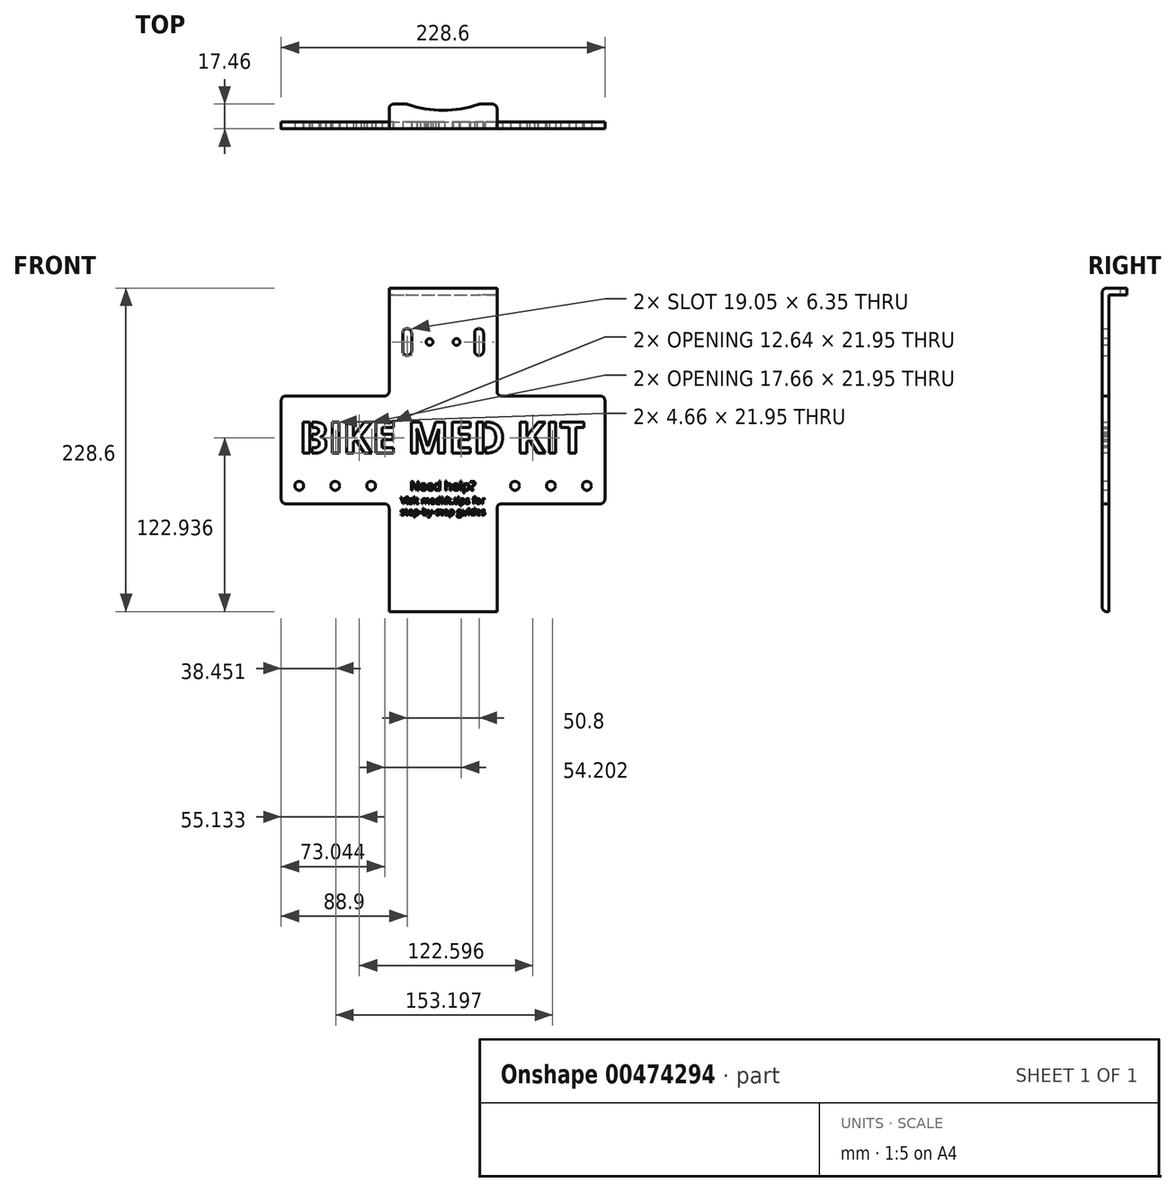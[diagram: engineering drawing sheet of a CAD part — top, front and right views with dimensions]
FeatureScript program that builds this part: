
annotation { "Feature Type Name" : "Feature", "Feature Type Description" : "" }
export const myFeature = defineFeature(function(context is Context, id is Id, definition is map)
    precondition{}
    {
        {
            var Q0;
            Q0=qCreatedBy(makeId("Front.planeOp"),FACE);
            var sketch = newSketch(context, id + "F0", { "sketchPlane" : qUnion([Q0])});
            skLineSegment(sketch, "E0.bottom", {"start": v(-38.1, 114.3) * mm, "end": v(38.1, 114.3) * mm});
            skLineSegment(sketch, "E0.top", {"start": v(-38.1, -114.3) * mm, "end": v(38.1, -114.3) * mm});
            skLineSegment(sketch, "E0.left", {"start": v(-38.1, 114.3) * mm, "end": v(-38.1, 38.1) * mm});
            skLineSegment(sketch, "E0.right", {"start": v(38.1, 114.3) * mm, "end": v(38.1, 38.1) * mm});
            skPoint(sketch, "E0.middle", {"position": v(0, 0) * mm});
            skLineSegment(sketch, "E1.bottom", {"start": v(114.3, 38.1) * mm, "end": v(38.1, 38.1) * mm});
            skLineSegment(sketch, "E1.top", {"start": v(114.3, -38.1) * mm, "end": v(38.1, -38.1) * mm});
            skLineSegment(sketch, "E1.left", {"start": v(114.3, 38.1) * mm, "end": v(114.3, -38.1) * mm});
            skLineSegment(sketch, "E1.right", {"start": v(-114.3, 38.1) * mm, "end": v(-114.3, -38.1) * mm});
            skLineSegment(sketch, "E2.trimOffspring", {"start": v(-38.1, 38.1) * mm, "end": v(-114.3, 38.1) * mm});
            skLineSegment(sketch, "E3.trimOffspring", {"start": v(-38.1, -38.1) * mm, "end": v(-38.1, -114.3) * mm});
            skLineSegment(sketch, "E4.trimOffspring", {"start": v(-38.1, -38.1) * mm, "end": v(-114.3, -38.1) * mm});
            skLineSegment(sketch, "E5.trimOffspring", {"start": v(38.1, -38.1) * mm, "end": v(38.1, -114.3) * mm});
            skSolve(sketch);
        }
        {
            var Q0;
            Q0=qSketchRegion(id+"F0",true);
            extrude(context, id + "F1", {"entities" : qUnion([Q0]), "oppositeDirection" : true, "depth" : 4.76 * mm});
        }
        {
            var Q0;
            Q0=makeQuery(id+"F1.opExtrude","CAP_FACE",FACE,{"disambiguationData":[OSD([sQuery(id+"F0.wireOp",EDGE,"E0.bottom"),sQuery(id+"F0.wireOp",EDGE,"E0.top"),sQuery(id+"F0.wireOp",EDGE,"E0.left"),sQuery(id+"F0.wireOp",EDGE,"E0.right"),sQuery(id+"F0.wireOp",EDGE,"E1.bottom"),sQuery(id+"F0.wireOp",EDGE,"E1.top"),sQuery(id+"F0.wireOp",EDGE,"E1.left"),sQuery(id+"F0.wireOp",EDGE,"E1.right"),sQuery(id+"F0.wireOp",EDGE,"E2.trimOffspring"),sQuery(id+"F0.wireOp",EDGE,"E3.trimOffspring"),sQuery(id+"F0.wireOp",EDGE,"E4.trimOffspring"),sQuery(id+"F0.wireOp",EDGE,"E5.trimOffspring")])],"isStart":true});
            var sketch = newSketch(context, id + "F2", { "sketchPlane" : qUnion([Q0])});
            skCircle(sketch, "E6", {"center": v(-101.6, -25.4) * mm, "radius": 3.18 * mm});
            skCircle(sketch, "E7.1.0.0", {"center": v(-76.2, -25.4) * mm, "radius": 3.18 * mm});
            skLineSegment(sketch, "E7.direction1", {"start": v(-101.6, -25.4) * mm, "end": v(-76.2, -25.4) * mm, "construction": true});
            skCircle(sketch, "E8", {"center": v(101.6, -25.4) * mm, "radius": 3.18 * mm});
            skCircle(sketch, "E9.1.0.0", {"center": v(76.2, -25.4) * mm, "radius": 3.18 * mm});
            skLineSegment(sketch, "E9.direction1", {"start": v(101.6, -25.4) * mm, "end": v(76.2, -25.4) * mm, "construction": true});
            skCircle(sketch, "E10.0.2.0", {"center": v(-50.8, -25.4) * mm, "radius": 3.18 * mm});
            skCircle(sketch, "E11.0.2.0", {"center": v(50.8, -25.4) * mm, "radius": 3.18 * mm});
            skSolve(sketch);
        }
        {
            var Q0;
            Q0=qSketchRegion(id+"F2",true);
            extrude(context, id + "F3", {"entities" : qUnion([Q0]), "operationType" : NewBodyOperationType.REMOVE, "endBound" : BoundingType.THROUGH_ALL, "oppositeDirection" : true, "depth" : 25.4 * mm});
        }
        {
            var Q0;
            Q0=makeQuery(id+"F1.opExtrude","CAP_FACE",FACE,{"disambiguationData":[OSD([sQuery(id+"F0.wireOp",EDGE,"E0.bottom"),sQuery(id+"F0.wireOp",EDGE,"E0.top"),sQuery(id+"F0.wireOp",EDGE,"E0.left"),sQuery(id+"F0.wireOp",EDGE,"E0.right"),sQuery(id+"F0.wireOp",EDGE,"E1.bottom"),sQuery(id+"F0.wireOp",EDGE,"E1.top"),sQuery(id+"F0.wireOp",EDGE,"E1.left"),sQuery(id+"F0.wireOp",EDGE,"E1.right"),sQuery(id+"F0.wireOp",EDGE,"E2.trimOffspring"),sQuery(id+"F0.wireOp",EDGE,"E3.trimOffspring"),sQuery(id+"F0.wireOp",EDGE,"E4.trimOffspring"),sQuery(id+"F0.wireOp",EDGE,"E5.trimOffspring")])],"isStart":true});
            var sketch = newSketch(context, id + "F4", { "sketchPlane" : qUnion([Q0])});
            skText(sketch, "E12", { "text": "BIKE MED KIT", "fontName": "OpenSans-Bold.ttf"});
            skLineSegment(sketch, "E13", {"start": v(-101.6, -22.23) * mm, "end": v(-76.2, -22.23) * mm, "construction": true});
            skLineSegment(sketch, "E14", {"start": v(-101.6, 7.94) * mm, "end": v(101.6, 7.94) * mm, "construction": true});
            const initialGuessF4  = {"E12": [-0.1016, -0.00234, 1, 0, 0.02214]};
            skSetInitialGuess(sketch, initialGuessF4);
            skSolve(sketch);
        }
        {
            var Q0;
            Q0=qSketchRegion(id+"F4",true);
            extrude(context, id + "F5", {"entities" : qUnion([Q0]), "operationType" : NewBodyOperationType.REMOVE, "endBound" : BoundingType.THROUGH_ALL, "oppositeDirection" : true, "depth" : 25.4 * mm});
        }
        {
            var Q0;
            {var subQ0=sQuery(id+"F0.wireOp",EDGE,"E2.trimOffspring");var subQ1=sQuery(id+"F0.wireOp",EDGE,"E1.right");var subQ2=sQuery(id+"F0.wireOp",EDGE,"E5.trimOffspring");var subQ3=sQuery(id+"F0.wireOp",EDGE,"E1.top");var subQ4=sQuery(id+"F0.wireOp",EDGE,"E1.left");var subQ5=sQuery(id+"F0.wireOp",EDGE,"E0.left");var subQ6=sQuery(id+"F0.wireOp",EDGE,"E1.bottom");var subQ7=sQuery(id+"F0.wireOp",EDGE,"E4.trimOffspring");var subQ8=sQuery(id+"F0.wireOp",EDGE,"E0.top");var subQ9=sQuery(id+"F0.wireOp",EDGE,"E0.right");var subQ10=sQuery(id+"F0.wireOp",EDGE,"E0.bottom");var subQ11=sQuery(id+"F0.wireOp",EDGE,"E3.trimOffspring");Q0=makeQuery(id+"F5.boolean.opBoolean","SPLIT",FACE,{"disambiguationData":[TD([makeQuery(id+"F1.opExtrude","SWEPT_FACE",FACE,{"disambiguationData":[OSD([subQ10])]})])],"derivedFrom":makeQuery(id+"F1.opExtrude","CAP_FACE",FACE,{"disambiguationData":[OSD([subQ10,subQ8,subQ5,subQ9,subQ6,subQ3,subQ4,subQ1,subQ0,subQ11,subQ7,subQ2])],"isStart":true})});}
            var sketch = newSketch(context, id + "F6", { "sketchPlane" : qUnion([Q0])});
            skLineSegment(sketch, "E15.bottom", {"start": v(-94.18, 23) * mm, "end": v(-92.6, 23) * mm});
            skLineSegment(sketch, "E15.top", {"start": v(-94.18, -7.38) * mm, "end": v(-92.6, -7.38) * mm});
            skLineSegment(sketch, "E15.left", {"start": v(-94.18, 23) * mm, "end": v(-94.18, -7.38) * mm});
            skLineSegment(sketch, "E15.right", {"start": v(-92.6, 23) * mm, "end": v(-92.6, -7.38) * mm});
            skLineSegment(sketch, "E16.bottom", {"start": v(28.49, 25.23) * mm, "end": v(30.07, 25.23) * mm});
            skLineSegment(sketch, "E16.top", {"start": v(28.49, -11.56) * mm, "end": v(30.07, -11.56) * mm});
            skLineSegment(sketch, "E16.left", {"start": v(28.49, 25.23) * mm, "end": v(28.49, -11.56) * mm});
            skLineSegment(sketch, "E16.right", {"start": v(30.07, 25.23) * mm, "end": v(30.07, -11.56) * mm});
            skSolve(sketch);
        }
        {
            var Q0;
            Q0=qSketchRegion(id+"F6",true);
            var Q1;
            {var subQ0=sQuery(id+"F0.wireOp",EDGE,"E2.trimOffspring");var subQ1=sQuery(id+"F0.wireOp",EDGE,"E1.right");var subQ2=sQuery(id+"F0.wireOp",EDGE,"E5.trimOffspring");var subQ3=sQuery(id+"F0.wireOp",EDGE,"E1.top");var subQ4=sQuery(id+"F0.wireOp",EDGE,"E1.left");var subQ5=sQuery(id+"F0.wireOp",EDGE,"E0.left");var subQ6=sQuery(id+"F0.wireOp",EDGE,"E1.bottom");var subQ7=sQuery(id+"F0.wireOp",EDGE,"E4.trimOffspring");var subQ8=sQuery(id+"F0.wireOp",EDGE,"E0.top");var subQ9=sQuery(id+"F0.wireOp",EDGE,"E0.right");var subQ10=sQuery(id+"F0.wireOp",EDGE,"E0.bottom");var subQ11=sQuery(id+"F0.wireOp",EDGE,"E3.trimOffspring");Q1=makeQuery(id+"F5.boolean.opBoolean","SPLIT",FACE,{"disambiguationData":[TD([makeQuery(id+"F1.opExtrude","SWEPT_FACE",FACE,{"disambiguationData":[OSD([subQ10])]})])],"derivedFrom":makeQuery(id+"F1.opExtrude","CAP_FACE",FACE,{"disambiguationData":[OSD([subQ10,subQ8,subQ5,subQ9,subQ6,subQ3,subQ4,subQ1,subQ0,subQ11,subQ7,subQ2])],"isStart":false})});}
            extrude(context, id + "F7", {"entities" : qUnion([Q0]), "operationType" : NewBodyOperationType.ADD, "endBound" : BoundingType.UP_TO_SURFACE, "oppositeDirection" : true, "endBoundEntityFace" : qUnion([Q1]), "depth" : 25.4 * mm});
        }
        {
            var Q0;
            {var subQ0=sQuery(id+"F0.wireOp",EDGE,"E5.trimOffspring");var subQ1=sQuery(id+"F0.wireOp",EDGE,"E4.trimOffspring");var subQ2=sQuery(id+"F0.wireOp",EDGE,"E3.trimOffspring");var subQ3=sQuery(id+"F0.wireOp",EDGE,"E2.trimOffspring");var subQ4=sQuery(id+"F0.wireOp",EDGE,"E1.right");var subQ5=sQuery(id+"F0.wireOp",EDGE,"E1.left");var subQ6=sQuery(id+"F0.wireOp",EDGE,"E1.top");var subQ7=sQuery(id+"F0.wireOp",EDGE,"E1.bottom");var subQ8=sQuery(id+"F0.wireOp",EDGE,"E0.right");var subQ9=sQuery(id+"F0.wireOp",EDGE,"E0.left");var subQ10=sQuery(id+"F0.wireOp",EDGE,"E0.top");var subQ11=sQuery(id+"F0.wireOp",EDGE,"E0.bottom");var subQ12=makeQuery(id+"F1.opExtrude","CAP_FACE",FACE,{"disambiguationData":[OSD([subQ11,subQ10,subQ9,subQ8,subQ7,subQ6,subQ5,subQ4,subQ3,subQ2,subQ1,subQ0])],"isStart":true});Q0=makeQuery(id+"F7.boolean.opBoolean","MERGE",FACE,{"derivedFrom":[makeQuery(id+"F5.boolean.opBoolean","SPLIT",FACE,{"disambiguationData":[TD([makeQuery(id+"F1.opExtrude","SWEPT_FACE",FACE,{"disambiguationData":[OSD([subQ11])]})])],"derivedFrom":subQ12}),makeQuery(id+"F5.boolean.opBoolean","SPLIT",FACE,{"disambiguationData":[TD([makeQuery(id+"F5.opExtrude","SWEPT_FACE",FACE,{"disambiguationData":[OSD([sQuery(id+"F4.wireOp",EDGE,"E12.sketch_text.stroke-12")])]})])],"derivedFrom":subQ12}),makeQuery(id+"F5.boolean.opBoolean","SPLIT",FACE,{"disambiguationData":[TD([makeQuery(id+"F5.opExtrude","SWEPT_FACE",FACE,{"disambiguationData":[OSD([sQuery(id+"F4.wireOp",EDGE,"E12.sketch_text.stroke-19")])]})])],"derivedFrom":subQ12}),makeQuery(id+"F5.boolean.opBoolean","SPLIT",FACE,{"disambiguationData":[TD([makeQuery(id+"F5.opExtrude","SWEPT_FACE",FACE,{"disambiguationData":[OSD([sQuery(id+"F4.wireOp",EDGE,"E12.sketch_text.stroke-92")])]})])],"derivedFrom":subQ12}),makeQuery(id+"F7.opExtrude","CAP_FACE",FACE,{"disambiguationData":[OSD([sQuery(id+"F6.wireOp",EDGE,"E15.bottom"),sQuery(id+"F6.wireOp",EDGE,"E15.top"),sQuery(id+"F6.wireOp",EDGE,"E15.left"),sQuery(id+"F6.wireOp",EDGE,"E15.right")])],"isStart":true}),makeQuery(id+"F7.opExtrude","CAP_FACE",FACE,{"disambiguationData":[OSD([sQuery(id+"F6.wireOp",EDGE,"E16.bottom"),sQuery(id+"F6.wireOp",EDGE,"E16.top"),sQuery(id+"F6.wireOp",EDGE,"E16.left"),sQuery(id+"F6.wireOp",EDGE,"E16.right")])],"isStart":true})]});}
            var sketch = newSketch(context, id + "F8", { "sketchPlane" : qUnion([Q0])});
            skLineSegment(sketch, "E17.bottom", {"start": v(-28.57, 85.73) * mm, "end": v(-22.22, 85.73) * mm});
            skLineSegment(sketch, "E17.top", {"start": v(-28.57, 66.68) * mm, "end": v(-22.22, 66.68) * mm});
            skLineSegment(sketch, "E17.left", {"start": v(-28.57, 85.73) * mm, "end": v(-28.57, 66.68) * mm});
            skLineSegment(sketch, "E17.right", {"start": v(-22.22, 85.73) * mm, "end": v(-22.22, 66.68) * mm});
            skLineSegment(sketch, "E18.MirrorCS", {"start": v(22.22, 85.73) * mm, "end": v(22.22, 66.68) * mm});
            skLineSegment(sketch, "E19.MirrorCS", {"start": v(28.57, 66.67) * mm, "end": v(22.22, 66.67) * mm});
            skLineSegment(sketch, "E20.MirrorCS", {"start": v(28.57, 85.73) * mm, "end": v(28.57, 66.67) * mm});
            skLineSegment(sketch, "E21.MirrorCS", {"start": v(28.57, 85.73) * mm, "end": v(22.22, 85.73) * mm});
            skLineSegment(sketch, "E22", {"start": v(-28.57, 76.2) * mm, "end": v(-22.22, 76.2) * mm, "construction": true});
            skLineSegment(sketch, "E23", {"start": v(-25.4, 85.73) * mm, "end": v(-25.4, 66.68) * mm, "construction": true});
            skSolve(sketch);
        }
        {
            var Q0;
            Q0=qSketchRegion(id+"F8",true);
            extrude(context, id + "F9", {"entities" : qUnion([Q0]), "operationType" : NewBodyOperationType.REMOVE, "endBound" : BoundingType.THROUGH_ALL, "oppositeDirection" : true, "depth" : 25.4 * mm});
        }
        {
            var Q0;
            Q0=makeQuery(id+"F9.boolean.opBoolean","COPY",EDGE,{"derivedFrom":makeQuery(id+"F9.opExtrude","SWEPT_EDGE",EDGE,{"disambiguationData":[OSD([sQuery(id+"F8.wireOp",EDGE,"E17.top"),sQuery(id+"F8.wireOp",EDGE,"E17.left")])]})});
            var Q1;
            Q1=makeQuery(id+"F9.boolean.opBoolean","COPY",EDGE,{"derivedFrom":makeQuery(id+"F9.opExtrude","SWEPT_EDGE",EDGE,{"disambiguationData":[OSD([sQuery(id+"F8.wireOp",EDGE,"E17.top"),sQuery(id+"F8.wireOp",EDGE,"E17.right")])]})});
            var Q2;
            Q2=makeQuery(id+"F9.boolean.opBoolean","COPY",EDGE,{"derivedFrom":makeQuery(id+"F9.opExtrude","SWEPT_EDGE",EDGE,{"disambiguationData":[OSD([sQuery(id+"F8.wireOp",EDGE,"E19.MirrorCS"),sQuery(id+"F8.wireOp",EDGE,"E20.MirrorCS")])]})});
            var Q3;
            Q3=makeQuery(id+"F9.boolean.opBoolean","COPY",EDGE,{"derivedFrom":makeQuery(id+"F9.opExtrude","SWEPT_EDGE",EDGE,{"disambiguationData":[OSD([sQuery(id+"F8.wireOp",EDGE,"E18.MirrorCS"),sQuery(id+"F8.wireOp",EDGE,"E19.MirrorCS")])]})});
            var Q4;
            Q4=makeQuery(id+"F9.boolean.opBoolean","COPY",EDGE,{"derivedFrom":makeQuery(id+"F9.opExtrude","SWEPT_EDGE",EDGE,{"disambiguationData":[OSD([sQuery(id+"F8.wireOp",EDGE,"E18.MirrorCS"),sQuery(id+"F8.wireOp",EDGE,"E21.MirrorCS")])]})});
            var Q5;
            Q5=makeQuery(id+"F9.boolean.opBoolean","COPY",EDGE,{"derivedFrom":makeQuery(id+"F9.opExtrude","SWEPT_EDGE",EDGE,{"disambiguationData":[OSD([sQuery(id+"F8.wireOp",EDGE,"E17.bottom"),sQuery(id+"F8.wireOp",EDGE,"E17.left")])]})});
            var Q6;
            Q6=makeQuery(id+"F9.boolean.opBoolean","COPY",EDGE,{"derivedFrom":makeQuery(id+"F9.opExtrude","SWEPT_EDGE",EDGE,{"disambiguationData":[OSD([sQuery(id+"F8.wireOp",EDGE,"E17.bottom"),sQuery(id+"F8.wireOp",EDGE,"E17.right")])]})});
            var Q7;
            Q7=makeQuery(id+"F9.boolean.opBoolean","COPY",EDGE,{"derivedFrom":makeQuery(id+"F9.opExtrude","SWEPT_EDGE",EDGE,{"disambiguationData":[OSD([sQuery(id+"F8.wireOp",EDGE,"E20.MirrorCS"),sQuery(id+"F8.wireOp",EDGE,"E21.MirrorCS")])]})});
            fillet(context, id + "F10", {"entities" : qUnion([Q0, Q1, Q2, Q3, Q4, Q5, Q6, Q7]), "radius" : 3.17 * mm, "tangentPropagation" : true, "allowEdgeOverflow" : false});
        }
        {
            var Q0;
            {var subQ0=sQuery(id+"F0.wireOp",EDGE,"E5.trimOffspring");var subQ1=sQuery(id+"F0.wireOp",EDGE,"E4.trimOffspring");var subQ2=sQuery(id+"F0.wireOp",EDGE,"E3.trimOffspring");var subQ3=sQuery(id+"F0.wireOp",EDGE,"E2.trimOffspring");var subQ4=sQuery(id+"F0.wireOp",EDGE,"E1.right");var subQ5=sQuery(id+"F0.wireOp",EDGE,"E1.left");var subQ6=sQuery(id+"F0.wireOp",EDGE,"E1.top");var subQ7=sQuery(id+"F0.wireOp",EDGE,"E1.bottom");var subQ8=sQuery(id+"F0.wireOp",EDGE,"E0.right");var subQ9=sQuery(id+"F0.wireOp",EDGE,"E0.left");var subQ10=sQuery(id+"F0.wireOp",EDGE,"E0.top");var subQ11=sQuery(id+"F0.wireOp",EDGE,"E0.bottom");var subQ12=makeQuery(id+"F1.opExtrude","CAP_FACE",FACE,{"disambiguationData":[OSD([subQ11,subQ10,subQ9,subQ8,subQ7,subQ6,subQ5,subQ4,subQ3,subQ2,subQ1,subQ0])],"isStart":true});Q0=makeQuery(id+"F7.boolean.opBoolean","MERGE",FACE,{"derivedFrom":[makeQuery(id+"F5.boolean.opBoolean","SPLIT",FACE,{"disambiguationData":[TD([makeQuery(id+"F1.opExtrude","SWEPT_FACE",FACE,{"disambiguationData":[OSD([subQ11])]})])],"derivedFrom":subQ12}),makeQuery(id+"F5.boolean.opBoolean","SPLIT",FACE,{"disambiguationData":[TD([makeQuery(id+"F5.opExtrude","SWEPT_FACE",FACE,{"disambiguationData":[OSD([sQuery(id+"F4.wireOp",EDGE,"E12.sketch_text.stroke-12")])]})])],"derivedFrom":subQ12}),makeQuery(id+"F5.boolean.opBoolean","SPLIT",FACE,{"disambiguationData":[TD([makeQuery(id+"F5.opExtrude","SWEPT_FACE",FACE,{"disambiguationData":[OSD([sQuery(id+"F4.wireOp",EDGE,"E12.sketch_text.stroke-19")])]})])],"derivedFrom":subQ12}),makeQuery(id+"F5.boolean.opBoolean","SPLIT",FACE,{"disambiguationData":[TD([makeQuery(id+"F5.opExtrude","SWEPT_FACE",FACE,{"disambiguationData":[OSD([sQuery(id+"F4.wireOp",EDGE,"E12.sketch_text.stroke-92")])]})])],"derivedFrom":subQ12}),makeQuery(id+"F7.opExtrude","CAP_FACE",FACE,{"disambiguationData":[OSD([sQuery(id+"F6.wireOp",EDGE,"E15.bottom"),sQuery(id+"F6.wireOp",EDGE,"E15.top"),sQuery(id+"F6.wireOp",EDGE,"E15.left"),sQuery(id+"F6.wireOp",EDGE,"E15.right")])],"isStart":true}),makeQuery(id+"F7.opExtrude","CAP_FACE",FACE,{"disambiguationData":[OSD([sQuery(id+"F6.wireOp",EDGE,"E16.bottom"),sQuery(id+"F6.wireOp",EDGE,"E16.top"),sQuery(id+"F6.wireOp",EDGE,"E16.left"),sQuery(id+"F6.wireOp",EDGE,"E16.right")])],"isStart":true})]});}
            var sketch = newSketch(context, id + "F11", { "sketchPlane" : qUnion([Q0])});
            skCircle(sketch, "E24", {"center": v(-9.53, 76.2) * mm, "radius": 2.38 * mm});
            skCircle(sketch, "E25", {"center": v(9.53, 76.2) * mm, "radius": 2.38 * mm});
            skLineSegment(sketch, "E26", {"start": v(-22.22, 76.2) * mm, "end": v(22.22, 76.2) * mm, "construction": true});
            skSolve(sketch);
        }
        {
            var Q0;
            Q0=qSketchRegion(id+"F11",true);
            extrude(context, id + "F12", {"entities" : qUnion([Q0]), "operationType" : NewBodyOperationType.REMOVE, "endBound" : BoundingType.THROUGH_ALL, "oppositeDirection" : true, "depth" : 25.4 * mm});
        }
        {
            var Q0;
            {var subQ0=sQuery(id+"F0.wireOp",EDGE,"E5.trimOffspring");var subQ1=sQuery(id+"F0.wireOp",EDGE,"E4.trimOffspring");var subQ2=sQuery(id+"F0.wireOp",EDGE,"E3.trimOffspring");var subQ3=sQuery(id+"F0.wireOp",EDGE,"E2.trimOffspring");var subQ4=sQuery(id+"F0.wireOp",EDGE,"E1.right");var subQ5=sQuery(id+"F0.wireOp",EDGE,"E1.left");var subQ6=sQuery(id+"F0.wireOp",EDGE,"E1.top");var subQ7=sQuery(id+"F0.wireOp",EDGE,"E1.bottom");var subQ8=sQuery(id+"F0.wireOp",EDGE,"E0.right");var subQ9=sQuery(id+"F0.wireOp",EDGE,"E0.left");var subQ10=sQuery(id+"F0.wireOp",EDGE,"E0.top");var subQ11=sQuery(id+"F0.wireOp",EDGE,"E0.bottom");var subQ12=makeQuery(id+"F1.opExtrude","CAP_FACE",FACE,{"disambiguationData":[OSD([subQ11,subQ10,subQ9,subQ8,subQ7,subQ6,subQ5,subQ4,subQ3,subQ2,subQ1,subQ0])],"isStart":true});Q0=makeQuery(id+"F7.boolean.opBoolean","MERGE",FACE,{"derivedFrom":[makeQuery(id+"F5.boolean.opBoolean","SPLIT",FACE,{"disambiguationData":[TD([makeQuery(id+"F1.opExtrude","SWEPT_FACE",FACE,{"disambiguationData":[OSD([subQ11])]})])],"derivedFrom":subQ12}),makeQuery(id+"F5.boolean.opBoolean","SPLIT",FACE,{"disambiguationData":[TD([makeQuery(id+"F5.opExtrude","SWEPT_FACE",FACE,{"disambiguationData":[OSD([sQuery(id+"F4.wireOp",EDGE,"E12.sketch_text.stroke-12")])]})])],"derivedFrom":subQ12}),makeQuery(id+"F5.boolean.opBoolean","SPLIT",FACE,{"disambiguationData":[TD([makeQuery(id+"F5.opExtrude","SWEPT_FACE",FACE,{"disambiguationData":[OSD([sQuery(id+"F4.wireOp",EDGE,"E12.sketch_text.stroke-19")])]})])],"derivedFrom":subQ12}),makeQuery(id+"F5.boolean.opBoolean","SPLIT",FACE,{"disambiguationData":[TD([makeQuery(id+"F5.opExtrude","SWEPT_FACE",FACE,{"disambiguationData":[OSD([sQuery(id+"F4.wireOp",EDGE,"E12.sketch_text.stroke-92")])]})])],"derivedFrom":subQ12}),makeQuery(id+"F7.opExtrude","CAP_FACE",FACE,{"disambiguationData":[OSD([sQuery(id+"F6.wireOp",EDGE,"E15.bottom"),sQuery(id+"F6.wireOp",EDGE,"E15.top"),sQuery(id+"F6.wireOp",EDGE,"E15.left"),sQuery(id+"F6.wireOp",EDGE,"E15.right")])],"isStart":true}),makeQuery(id+"F7.opExtrude","CAP_FACE",FACE,{"disambiguationData":[OSD([sQuery(id+"F6.wireOp",EDGE,"E16.bottom"),sQuery(id+"F6.wireOp",EDGE,"E16.top"),sQuery(id+"F6.wireOp",EDGE,"E16.left"),sQuery(id+"F6.wireOp",EDGE,"E16.right")])],"isStart":true})]});}
            var sketch = newSketch(context, id + "F13", { "sketchPlane" : qUnion([Q0])});
            skText(sketch, "E27", { "text": "Need help?", "fontName": "OpenSans-Regular.ttf"});
            skText(sketch, "E28", { "text": "Visit medkit.tips for", "fontName": "OpenSans-Regular.ttf"});
            skText(sketch, "E29", { "text": "step-by-step guides", "fontName": "OpenSans-Regular.ttf"});
            const initialGuessF13  = {"E27": [-0.02318, -0.02858, 1, 0, 0.00635], "E28": [-0.02993, -0.0381, 1, 0, 0.00476], "E29": [-0.03014, -0.04604, 1, 0, 0.00476]};
            skSetInitialGuess(sketch, initialGuessF13);
            skSolve(sketch);
        }
        {
            var Q0;
            Q0=qSketchRegion(id+"F13",true);
            var Q1;
            Q1=qConstructionFilter(qBodyType(qCreatedBy(id+"F13",EDGE),BodyType.WIRE),ConstructionObject.NO);
            extrude(context, id + "F14", {"entities" : qUnion([Q0]), "operationType" : NewBodyOperationType.REMOVE, "surfaceEntities" : qUnion([Q1]), "oppositeDirection" : true, "depth" : 0.03 * mm});
        }
        {
            var Q0;
            Q0=makeQuery(id+"F1.opExtrude","SWEPT_FACE",FACE,{"disambiguationData":[OSD([sQuery(id+"F0.wireOp",EDGE,"E0.bottom")])]});
            var sketch = newSketch(context, id + "F15", { "sketchPlane" : qUnion([Q0])});
            skLineSegment(sketch, "E30", {"start": v(-38.1, 4.76) * mm, "end": v(-38.1, 17.46) * mm});
            skLineSegment(sketch, "E31", {"start": v(-38.1, 17.46) * mm, "end": v(-25.4, 17.46) * mm});
            skLineSegment(sketch, "E32", {"start": v(38.1, 4.76) * mm, "end": v(-38.1, 4.76) * mm});
            skLineSegment(sketch, "E33", {"start": v(38.1, 4.76) * mm, "end": v(38.1, 17.46) * mm});
            skLineSegment(sketch, "E34", {"start": v(38.1, 17.46) * mm, "end": v(25.4, 17.46) * mm});
            skArc(sketch, "E35", {"start": v(-25.4, 17.46) * mm, "mid": v(0, 13.1) * mm, "end": v(25.4, 17.46) * mm});
            skLineSegment(sketch, "E36", {"start": v(0, 4.76) * mm, "end": v(0, 89.3) * mm, "construction": true});
            skPoint(sketch, "E36.startSnap0", {"position": v(0, 4.76) * mm});
            skSolve(sketch);
        }
        {
            var Q0;
            Q0 = qSketchRegion(id + "F15", true);
            extrude(context, id + "F16", {"entities" : qUnion([Q0]), "operationType" : NewBodyOperationType.ADD, "oppositeDirection" : true, "depth" : 4.76 * mm});
        }
        {
            var Q0;
            Q0=makeQuery(id+"F1.opExtrude","SWEPT_EDGE",EDGE,{"disambiguationData":[OSD([sQuery(id+"F0.wireOp",EDGE,"E0.right"),sQuery(id+"F0.wireOp",EDGE,"E1.bottom")])]});
            var Q1;
            Q1=makeQuery(id+"F1.opExtrude","SWEPT_EDGE",EDGE,{"disambiguationData":[OSD([sQuery(id+"F0.wireOp",EDGE,"E1.bottom"),sQuery(id+"F0.wireOp",EDGE,"E1.left")])]});
            var Q2;
            Q2=makeQuery(id+"F1.opExtrude","SWEPT_EDGE",EDGE,{"disambiguationData":[OSD([sQuery(id+"F0.wireOp",EDGE,"E1.top"),sQuery(id+"F0.wireOp",EDGE,"E1.left")])]});
            var Q3;
            Q3=makeQuery(id+"F1.opExtrude","SWEPT_EDGE",EDGE,{"disambiguationData":[OSD([sQuery(id+"F0.wireOp",EDGE,"E1.right"),sQuery(id+"F0.wireOp",EDGE,"E2.trimOffspring")])]});
            var Q4;
            Q4=makeQuery(id+"F1.opExtrude","SWEPT_EDGE",EDGE,{"disambiguationData":[OSD([sQuery(id+"F0.wireOp",EDGE,"E1.right"),sQuery(id+"F0.wireOp",EDGE,"E4.trimOffspring")])]});
            var Q5;
            Q5=makeQuery(id+"F1.opExtrude","SWEPT_EDGE",EDGE,{"disambiguationData":[OSD([sQuery(id+"F0.wireOp",EDGE,"E3.trimOffspring"),sQuery(id+"F0.wireOp",EDGE,"E4.trimOffspring")])]});
            var Q6;
            Q6=makeQuery(id+"F1.opExtrude","SWEPT_EDGE",EDGE,{"disambiguationData":[OSD([sQuery(id+"F0.wireOp",EDGE,"E1.top"),sQuery(id+"F0.wireOp",EDGE,"E5.trimOffspring")])]});
            var Q7;
            Q7=makeQuery(id+"F1.opExtrude","SWEPT_EDGE",EDGE,{"disambiguationData":[OSD([sQuery(id+"F0.wireOp",EDGE,"E0.left"),sQuery(id+"F0.wireOp",EDGE,"E2.trimOffspring")])]});
            var Q8;
            Q8=makeQuery(id+"F1.opExtrude","CAP_EDGE",EDGE,{"disambiguationData":[OSD([sQuery(id+"F0.wireOp",EDGE,"E0.bottom")])],"isStart":true});
            var Q9;
            Q9=makeQuery(id+"F16.opExtrude","SWEPT_EDGE",EDGE,{"disambiguationData":[OSD([sQuery(id+"F15.wireOp",EDGE,"E33"),sQuery(id+"F15.wireOp",EDGE,"E34")])]});
            var Q10;
            Q10=makeQuery(id+"F16.opExtrude","SWEPT_EDGE",EDGE,{"disambiguationData":[OSD([sQuery(id+"F15.wireOp",EDGE,"E34"),sQuery(id+"F15.wireOp",EDGE,"E35")])]});
            var Q11;
            Q11=makeQuery(id+"F16.opExtrude","SWEPT_EDGE",EDGE,{"disambiguationData":[OSD([sQuery(id+"F15.wireOp",EDGE,"E31"),sQuery(id+"F15.wireOp",EDGE,"E35")])]});
            var Q12;
            Q12=makeQuery(id+"F16.opExtrude","SWEPT_EDGE",EDGE,{"disambiguationData":[OSD([sQuery(id+"F15.wireOp",EDGE,"E30"),sQuery(id+"F15.wireOp",EDGE,"E31")])]});
            var Q13;
            Q13=makeQuery(id+"FCWQdBFXLMpHDpm_1.1.F16.opExtrude","SWEPT_EDGE",EDGE,{"disambiguationData":[OSD([sQuery(id+"F15.wireOp",EDGE,"E33"),sQuery(id+"F15.wireOp",EDGE,"E34")])]});
            var Q14;
            Q14=makeQuery(id+"FCWQdBFXLMpHDpm_1.1.F16.opExtrude","SWEPT_EDGE",EDGE,{"disambiguationData":[OSD([sQuery(id+"F15.wireOp",EDGE,"E34"),sQuery(id+"F15.wireOp",EDGE,"E35")])]});
            var Q15;
            Q15=makeQuery(id+"FCWQdBFXLMpHDpm_1.1.F16.opExtrude","SWEPT_EDGE",EDGE,{"disambiguationData":[OSD([sQuery(id+"F15.wireOp",EDGE,"E31"),sQuery(id+"F15.wireOp",EDGE,"E35")])]});
            var Q16;
            Q16=makeQuery(id+"FCWQdBFXLMpHDpm_1.1.F16.opExtrude","SWEPT_EDGE",EDGE,{"disambiguationData":[OSD([sQuery(id+"F15.wireOp",EDGE,"E30"),sQuery(id+"F15.wireOp",EDGE,"E31")])]});
            var Q17;
            Q17=makeQuery(id+"F1.opExtrude","CAP_EDGE",EDGE,{"disambiguationData":[OSD([sQuery(id+"F0.wireOp",EDGE,"E0.top")])],"isStart":true});
            fillet(context, id + "F17", {"entities" : qUnion([Q0, Q1, Q2, Q3, Q4, Q5, Q6, Q7, Q8, Q9, Q10, Q11, Q12, Q13, Q14, Q15, Q16, Q17]), "radius" : 3.17 * mm, "tangentPropagation" : true, "allowEdgeOverflow" : false});
        }
    });
